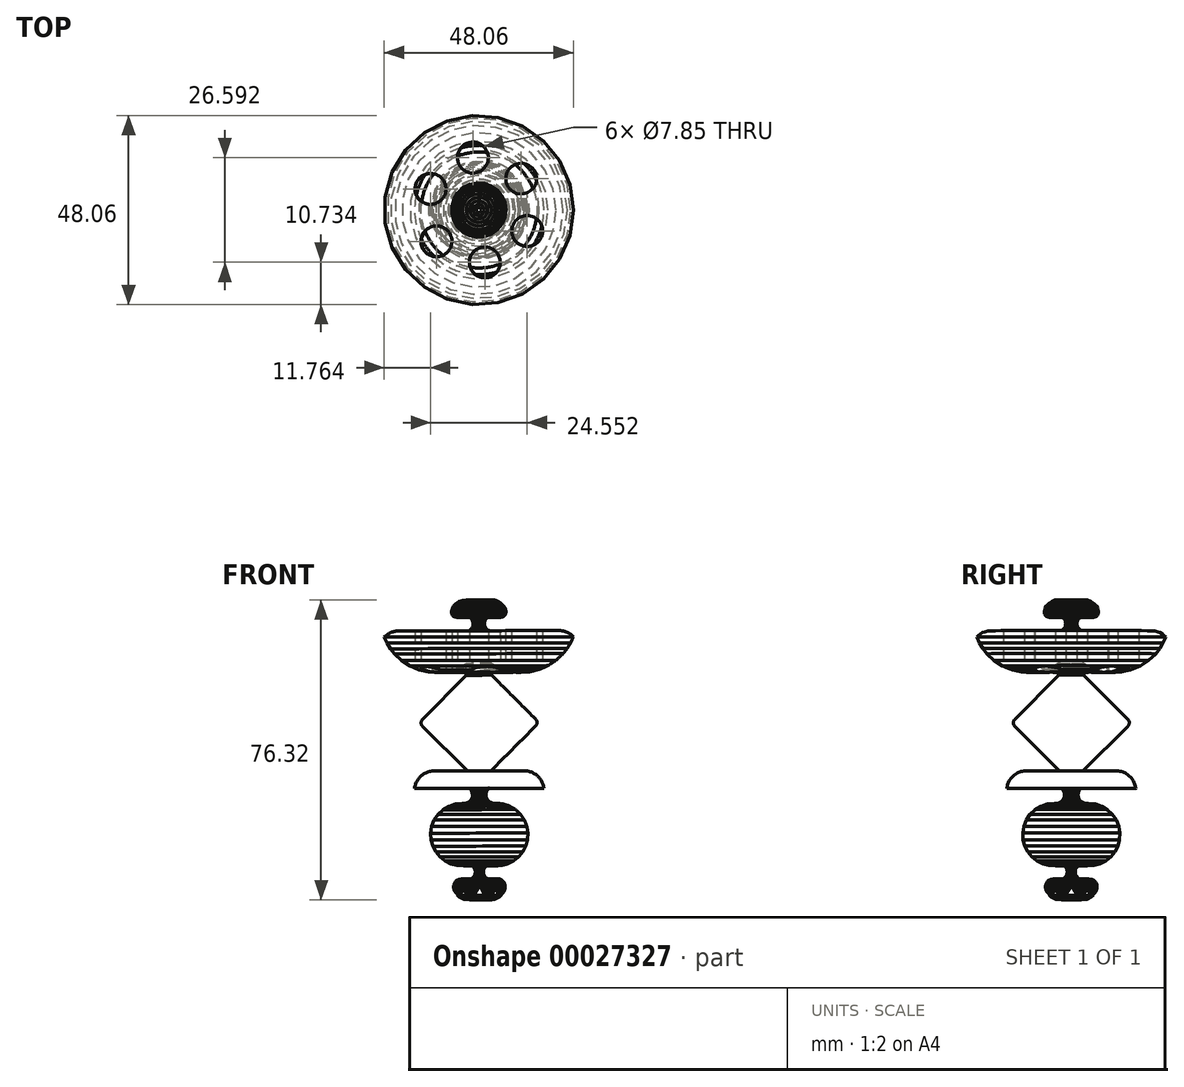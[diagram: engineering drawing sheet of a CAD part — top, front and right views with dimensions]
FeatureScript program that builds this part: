
annotation { "Feature Type Name" : "Feature", "Feature Type Description" : "" }
export const myFeature = defineFeature(function(context is Context, id is Id, definition is map)
    precondition{}
    {
        {
            var Q0;
            Q0=qCreatedBy(makeId("Front.planeOp"),FACE);
            var sketch = newSketch(context, id + "F0", { "sketchPlane" : qUnion([Q0])});
            skLineSegment(sketch, "E0", {"start": v(-12.1, 32.41) * mm, "end": v(-11.6, 14.99) * mm});
            skLineSegment(sketch, "E1", {"start": v(-11.6, 14.99) * mm, "end": v(-11.42, -2.45) * mm});
            skLineSegment(sketch, "E2", {"start": v(-11.42, -2.45) * mm, "end": v(-11.6, -19.88) * mm});
            skLineSegment(sketch, "E3", {"start": v(-11.6, -19.88) * mm, "end": v(-12.1, -37.31) * mm});
            skLineSegment(sketch, "E4", {"start": v(-12.1, -37.31) * mm, "end": v(-10.88, -37.94) * mm});
            skLineSegment(sketch, "E5", {"start": v(-10.88, -37.94) * mm, "end": v(-9.52, -38.15) * mm});
            skLineSegment(sketch, "E6", {"start": v(-9.52, -38.15) * mm, "end": v(-8.17, -37.94) * mm});
            skLineSegment(sketch, "E7", {"start": v(-8.17, -37.94) * mm, "end": v(-6.94, -37.31) * mm});
            skLineSegment(sketch, "E8", {"start": v(-6.94, -37.31) * mm, "end": v(-6.41, -36.86) * mm});
            skLineSegment(sketch, "E9", {"start": v(-6.41, -36.86) * mm, "end": v(-5.98, -36.31) * mm});
            skLineSegment(sketch, "E10", {"start": v(-5.98, -36.31) * mm, "end": v(-5.68, -35.68) * mm});
            skLineSegment(sketch, "E11", {"start": v(-5.68, -35.68) * mm, "end": v(-5.55, -35) * mm});
            skLineSegment(sketch, "E12", {"start": v(-5.55, -35) * mm, "end": v(-5.6, -34.31) * mm});
            skLineSegment(sketch, "E13", {"start": v(-5.6, -34.31) * mm, "end": v(-5.86, -33.67) * mm});
            skLineSegment(sketch, "E14", {"start": v(-5.86, -33.67) * mm, "end": v(-6.07, -33.4) * mm});
            skLineSegment(sketch, "E15", {"start": v(-6.07, -33.4) * mm, "end": v(-6.33, -33.15) * mm});
            skLineSegment(sketch, "E16", {"start": v(-6.33, -33.15) * mm, "end": v(-6.62, -32.97) * mm});
            skLineSegment(sketch, "E17", {"start": v(-6.62, -32.97) * mm, "end": v(-6.94, -32.84) * mm});
            skLineSegment(sketch, "E18", {"start": v(-6.94, -32.84) * mm, "end": v(-7.62, -32.76) * mm});
            skLineSegment(sketch, "E19", {"start": v(-7.62, -32.76) * mm, "end": v(-8.32, -32.82) * mm});
            skLineSegment(sketch, "E20", {"start": v(-8.32, -32.82) * mm, "end": v(-9, -32.9) * mm});
            skLineSegment(sketch, "E21", {"start": v(-9, -32.9) * mm, "end": v(-9.7, -32.84) * mm});
            skLineSegment(sketch, "E22", {"start": v(-9.7, -32.84) * mm, "end": v(-10.26, -32.6) * mm});
            skLineSegment(sketch, "E23", {"start": v(-10.26, -32.6) * mm, "end": v(-10.72, -32.18) * mm});
            skLineSegment(sketch, "E24", {"start": v(-10.72, -32.18) * mm, "end": v(-11.02, -31.64) * mm});
            skLineSegment(sketch, "E25", {"start": v(-11.02, -31.64) * mm, "end": v(-11.12, -31.03) * mm});
            skLineSegment(sketch, "E26", {"start": v(-11.12, -31.03) * mm, "end": v(-11.02, -30.42) * mm});
            skLineSegment(sketch, "E27", {"start": v(-11.02, -30.42) * mm, "end": v(-10.72, -29.88) * mm});
            skLineSegment(sketch, "E28", {"start": v(-10.72, -29.88) * mm, "end": v(-10.26, -29.46) * mm});
            skLineSegment(sketch, "E29", {"start": v(-10.26, -29.46) * mm, "end": v(-9.7, -29.22) * mm});
            skLineSegment(sketch, "E30", {"start": v(-9.7, -29.22) * mm, "end": v(-8.07, -29.46) * mm});
            skLineSegment(sketch, "E31", {"start": v(-8.07, -29.46) * mm, "end": v(-6.44, -29.35) * mm});
            skLineSegment(sketch, "E32", {"start": v(-6.44, -29.35) * mm, "end": v(-4.85, -28.93) * mm});
            skLineSegment(sketch, "E33", {"start": v(-4.85, -28.93) * mm, "end": v(-3.4, -28.19) * mm});
            skLineSegment(sketch, "E34", {"start": v(-3.4, -28.19) * mm, "end": v(-2.12, -27.15) * mm});
            skLineSegment(sketch, "E35", {"start": v(-2.12, -27.15) * mm, "end": v(-1.09, -25.88) * mm});
            skLineSegment(sketch, "E36", {"start": v(-1.09, -25.88) * mm, "end": v(-0.33, -24.43) * mm});
            skLineSegment(sketch, "E37", {"start": v(-0.33, -24.43) * mm, "end": v(0.12, -22.85) * mm});
            skLineSegment(sketch, "E38", {"start": v(0.12, -22.85) * mm, "end": v(0.22, -21.12) * mm});
            skLineSegment(sketch, "E39", {"start": v(0.22, -21.12) * mm, "end": v(-0.06, -19.4) * mm});
            skLineSegment(sketch, "E40", {"start": v(-0.06, -19.4) * mm, "end": v(-0.7, -17.79) * mm});
            skLineSegment(sketch, "E41", {"start": v(-0.7, -17.79) * mm, "end": v(-1.67, -16.35) * mm});
            skLineSegment(sketch, "E42", {"start": v(-1.67, -16.35) * mm, "end": v(-2.93, -15.17) * mm});
            skLineSegment(sketch, "E43", {"start": v(-2.93, -15.17) * mm, "end": v(-4.43, -14.28) * mm});
            skLineSegment(sketch, "E44", {"start": v(-4.43, -14.28) * mm, "end": v(-6.08, -13.73) * mm});
            skLineSegment(sketch, "E45", {"start": v(-6.08, -13.73) * mm, "end": v(-7.8, -13.55) * mm});
            skLineSegment(sketch, "E46", {"start": v(-7.8, -13.55) * mm, "end": v(-8.7, -13.56) * mm});
            skLineSegment(sketch, "E47", {"start": v(-8.7, -13.56) * mm, "end": v(-9.52, -13.2) * mm});
            skLineSegment(sketch, "E48", {"start": v(-9.52, -13.2) * mm, "end": v(-9.92, -12.86) * mm});
            skLineSegment(sketch, "E49", {"start": v(-9.92, -12.86) * mm, "end": v(-10.21, -12.42) * mm});
            skLineSegment(sketch, "E50", {"start": v(-10.21, -12.42) * mm, "end": v(-10.4, -11.93) * mm});
            skLineSegment(sketch, "E51", {"start": v(-10.4, -11.93) * mm, "end": v(-10.47, -11.4) * mm});
            skLineSegment(sketch, "E52", {"start": v(-10.47, -11.4) * mm, "end": v(-10.4, -10.88) * mm});
            skLineSegment(sketch, "E53", {"start": v(-10.4, -10.88) * mm, "end": v(-10.21, -10.38) * mm});
            skLineSegment(sketch, "E54", {"start": v(-10.21, -10.38) * mm, "end": v(-9.92, -9.95) * mm});
            skLineSegment(sketch, "E55", {"start": v(-9.92, -9.95) * mm, "end": v(-9.52, -9.6) * mm});
            skLineSegment(sketch, "E56", {"start": v(-9.52, -9.6) * mm, "end": v(4.25, -9.77) * mm});
            skLineSegment(sketch, "E57", {"start": v(4.25, -9.77) * mm, "end": v(4.42, -5.29) * mm});
            skLineSegment(sketch, "E58", {"start": v(4.42, -5.29) * mm, "end": v(-9.18, -5.29) * mm});
            skLineSegment(sketch, "E59", {"start": v(-9.18, -5.29) * mm, "end": v(3.05, 6.93) * mm});
            skLineSegment(sketch, "E60", {"start": v(3.05, 6.93) * mm, "end": v(-9, 18.99) * mm});
            skLineSegment(sketch, "E61", {"start": v(-9, 18.99) * mm, "end": v(-9, 21.91) * mm});
            skLineSegment(sketch, "E62", {"start": v(-9, 21.91) * mm, "end": v(-6.8, 20.77) * mm});
            skLineSegment(sketch, "E63", {"start": v(-6.8, 20.77) * mm, "end": v(-4.4, 20.03) * mm});
            skLineSegment(sketch, "E64", {"start": v(-4.4, 20.03) * mm, "end": v(-1.93, 19.71) * mm});
            skLineSegment(sketch, "E65", {"start": v(-1.93, 19.71) * mm, "end": v(0.56, 19.84) * mm});
            skLineSegment(sketch, "E66", {"start": v(0.56, 19.84) * mm, "end": v(2.99, 20.4) * mm});
            skLineSegment(sketch, "E67", {"start": v(2.99, 20.4) * mm, "end": v(5.28, 21.4) * mm});
            skLineSegment(sketch, "E68", {"start": v(5.28, 21.4) * mm, "end": v(7.37, 22.76) * mm});
            skLineSegment(sketch, "E69", {"start": v(7.37, 22.76) * mm, "end": v(9.18, 24.48) * mm});
            skLineSegment(sketch, "E70", {"start": v(9.18, 24.48) * mm, "end": v(10.2, 25.8) * mm});
            skLineSegment(sketch, "E71", {"start": v(10.2, 25.8) * mm, "end": v(11.08, 27.23) * mm});
            skLineSegment(sketch, "E72", {"start": v(11.08, 27.23) * mm, "end": v(11.77, 28.75) * mm});
            skLineSegment(sketch, "E73", {"start": v(11.77, 28.75) * mm, "end": v(12.28, 30.35) * mm});
            skLineSegment(sketch, "E74", {"start": v(12.28, 30.35) * mm, "end": v(-9.18, 30.18) * mm});
            skLineSegment(sketch, "E75", {"start": v(-9.18, 30.18) * mm, "end": v(-9.52, 30.25) * mm});
            skLineSegment(sketch, "E76", {"start": v(-9.52, 30.25) * mm, "end": v(-9.83, 30.38) * mm});
            skLineSegment(sketch, "E77", {"start": v(-9.83, 30.38) * mm, "end": v(-10.12, 30.57) * mm});
            skLineSegment(sketch, "E78", {"start": v(-10.12, 30.57) * mm, "end": v(-10.38, 30.8) * mm});
            skLineSegment(sketch, "E79", {"start": v(-10.38, 30.8) * mm, "end": v(-10.58, 31.08) * mm});
            skLineSegment(sketch, "E80", {"start": v(-10.58, 31.08) * mm, "end": v(-10.73, 31.4) * mm});
            skLineSegment(sketch, "E81", {"start": v(-10.73, 31.4) * mm, "end": v(-10.82, 31.73) * mm});
            skLineSegment(sketch, "E82", {"start": v(-10.82, 31.73) * mm, "end": v(-10.86, 32.07) * mm});
            skLineSegment(sketch, "E83", {"start": v(-10.86, 32.07) * mm, "end": v(-10.82, 32.41) * mm});
            skLineSegment(sketch, "E84", {"start": v(-10.82, 32.41) * mm, "end": v(-10.73, 32.75) * mm});
            skLineSegment(sketch, "E85", {"start": v(-10.73, 32.75) * mm, "end": v(-10.58, 33.06) * mm});
            skLineSegment(sketch, "E86", {"start": v(-10.58, 33.06) * mm, "end": v(-10.38, 33.34) * mm});
            skLineSegment(sketch, "E87", {"start": v(-10.38, 33.34) * mm, "end": v(-10.12, 33.57) * mm});
            skLineSegment(sketch, "E88", {"start": v(-10.12, 33.57) * mm, "end": v(-9.83, 33.76) * mm});
            skLineSegment(sketch, "E89", {"start": v(-9.83, 33.76) * mm, "end": v(-9.52, 33.9) * mm});
            skLineSegment(sketch, "E90", {"start": v(-9.52, 33.9) * mm, "end": v(-9.18, 33.96) * mm});
            skLineSegment(sketch, "E91", {"start": v(-9.18, 33.96) * mm, "end": v(-8.35, 33.92) * mm});
            skLineSegment(sketch, "E92", {"start": v(-8.35, 33.92) * mm, "end": v(-7.52, 33.75) * mm});
            skLineSegment(sketch, "E93", {"start": v(-7.52, 33.75) * mm, "end": v(-6.69, 33.69) * mm});
            skLineSegment(sketch, "E94", {"start": v(-6.69, 33.69) * mm, "end": v(-6.28, 33.77) * mm});
            skLineSegment(sketch, "E95", {"start": v(-6.28, 33.77) * mm, "end": v(-5.9, 33.96) * mm});
            skLineSegment(sketch, "E96", {"start": v(-5.9, 33.96) * mm, "end": v(-5.66, 34.22) * mm});
            skLineSegment(sketch, "E97", {"start": v(-5.66, 34.22) * mm, "end": v(-5.48, 34.53) * mm});
            skLineSegment(sketch, "E98", {"start": v(-5.48, 34.53) * mm, "end": v(-5.39, 34.88) * mm});
            skLineSegment(sketch, "E99", {"start": v(-5.39, 34.88) * mm, "end": v(-5.38, 35.23) * mm});
            skLineSegment(sketch, "E100", {"start": v(-5.38, 35.23) * mm, "end": v(-5.55, 35.93) * mm});
            skLineSegment(sketch, "E101", {"start": v(-5.55, 35.93) * mm, "end": v(-5.9, 36.55) * mm});
            skLineSegment(sketch, "E102", {"start": v(-5.9, 36.55) * mm, "end": v(-6.54, 37.22) * mm});
            skLineSegment(sketch, "E103", {"start": v(-6.54, 37.22) * mm, "end": v(-7.31, 37.72) * mm});
            skLineSegment(sketch, "E104", {"start": v(-7.31, 37.72) * mm, "end": v(-8.18, 38.04) * mm});
            skLineSegment(sketch, "E105", {"start": v(-8.18, 38.04) * mm, "end": v(-9.1, 38.15) * mm});
            skLineSegment(sketch, "E106", {"start": v(-9.1, 38.15) * mm, "end": v(-10, 38.04) * mm});
            skLineSegment(sketch, "E107", {"start": v(-10, 38.04) * mm, "end": v(-10.87, 37.72) * mm});
            skLineSegment(sketch, "E108", {"start": v(-10.87, 37.72) * mm, "end": v(-11.64, 37.22) * mm});
            skLineSegment(sketch, "E109", {"start": v(-11.64, 37.22) * mm, "end": v(-12.28, 36.55) * mm});
            skLineSegment(sketch, "E110", {"start": v(-12.28, 36.55) * mm, "end": v(-12.1, 32.41) * mm});
            skLineSegment(sketch, "E111", {"start": v(-12.28, 36.55) * mm, "end": v(-12.1, -37.31) * mm});
            skSolve(sketch);
        }
        {
            var Q0;
            Q0 = qSketchRegion(id + "F0", true);
            var Q1;
            Q1=sQuery(id+"F0.wireOp",EDGE,"E111");
            revolve(context, id + "F1", {"entities" : qUnion([Q0]), "axis" : qUnion([Q1]), "revolveType" : RevolveType.FULL});
        }
        {
            var Q0;
            Q0=makeQuery(id+"F1.opRevolve","SWEPT_EDGE",EDGE,{"disambiguationData":[OSD([sQuery(id+"F0.wireOp",EDGE,"E73"),sQuery(id+"F0.wireOp",EDGE,"E74")])]});
            fillet(context, id + "F2", {"entities" : qUnion([Q0]), "radius" : 5.08 * mm, "tangentPropagation" : true, "allowEdgeOverflow" : false});
        }
        {
            var Q0;
            Q0=makeQuery(id+"F1.opRevolve","SWEPT_EDGE",EDGE,{"disambiguationData":[OSD([sQuery(id+"F0.wireOp",EDGE,"E57"),sQuery(id+"F0.wireOp",EDGE,"E58")])]});
            fillet(context, id + "F3", {"entities" : qUnion([Q0]), "radius" : 5.08 * mm, "tangentPropagation" : true, "allowEdgeOverflow" : false});
        }
        {
            var Q0;
            Q0=qCreatedBy(makeId("Top.planeOp"),FACE);
            var sketch = newSketch(context, id + "F4", { "sketchPlane" : qUnion([Q0])});
            skCircle(sketch, "E112", {"center": v(-47.8, 37.52) * mm, "radius": 3.93 * mm});
            skSolve(sketch);
        }
        {
            var Q0;
            Q0=makeQuery(id+"F4.imprint","IMPRINT",FACE,{"disambiguationData":[TD([[makeQuery(id+"F4.imprint","IMPRINT",EDGE,{"derivedFrom":sQuery(id+"F4.wireOp",EDGE,"E112")}),1.0]])]});
            extrude(context, id + "F5", {"entities" : qUnion([Q0]), "depth" : 12.7 * mm});
        }
        {
            var Q0;
            Q0=makeQuery(id+"F5.opExtrude","SWEPT_BODY",BODY,{"disambiguationData":[OSD([sQuery(id+"F4.wireOp",EDGE,"E112")])]});
            transform(context, id + "F6", {"entities" : qUnion([Q0]), "transformType" : TransformType.TRANSLATION_3D, "dx" : 46.3 * mm, "dy" : -29.56 * mm, "dz" : 18.45 * mm, "makeCopy" : false});
        }
        {
            var Q0;
            Q0=makeQuery(id+"F5.opExtrude","SWEPT_BODY",BODY,{"disambiguationData":[OSD([sQuery(id+"F4.wireOp",EDGE,"E112")])]});
            var Q1;
            Q1=makeQuery(id+"F2.opFillet","BLEND_EDGE",EDGE,{"blendedFrom":[makeQuery(id+"F1.opRevolve","SWEPT_EDGE",EDGE,{"disambiguationData":[OSD([sQuery(id+"F0.wireOp",EDGE,"E73"),sQuery(id+"F0.wireOp",EDGE,"E74")])]}),makeQuery(id+"F1.opRevolve","SWEPT_FACE",FACE,{"disambiguationData":[OSD([sQuery(id+"F0.wireOp",EDGE,"E72")])]})],"blendedInto":[makeQuery(id+"F1.opRevolve","SWEPT_FACE",FACE,{"disambiguationData":[OSD([sQuery(id+"F0.wireOp",EDGE,"E72")])]})]});
            circularPattern(context, id + "F7", {"entities" : qUnion([Q0]), "axis" : qUnion([Q1]), "angle" : 360 * degree, "instanceCount" : 6, "equalSpace" : true});
        }
        {
            var Q0;
            Q0=makeQuery(id+"F7.opPattern","COPY",BODY,{"derivedFrom":makeQuery(id+"F5.opExtrude","SWEPT_BODY",BODY,{"disambiguationData":[OSD([sQuery(id+"F4.wireOp",EDGE,"E112")])]}),"instanceName":"4"});
            var Q1;
            Q1=makeQuery(id+"F7.opPattern","COPY",BODY,{"derivedFrom":makeQuery(id+"F5.opExtrude","SWEPT_BODY",BODY,{"disambiguationData":[OSD([sQuery(id+"F4.wireOp",EDGE,"E112")])]}),"instanceName":"5"});
            var Q2;
            Q2=makeQuery(id+"F5.opExtrude","SWEPT_BODY",BODY,{"disambiguationData":[OSD([sQuery(id+"F4.wireOp",EDGE,"E112")])]});
            var Q3;
            Q3=makeQuery(id+"F7.opPattern","COPY",BODY,{"derivedFrom":makeQuery(id+"F5.opExtrude","SWEPT_BODY",BODY,{"disambiguationData":[OSD([sQuery(id+"F4.wireOp",EDGE,"E112")])]}),"instanceName":"1"});
            var Q4;
            Q4=makeQuery(id+"F7.opPattern","COPY",BODY,{"derivedFrom":makeQuery(id+"F5.opExtrude","SWEPT_BODY",BODY,{"disambiguationData":[OSD([sQuery(id+"F4.wireOp",EDGE,"E112")])]}),"instanceName":"2"});
            var Q5;
            Q5=makeQuery(id+"F7.opPattern","COPY",BODY,{"derivedFrom":makeQuery(id+"F5.opExtrude","SWEPT_BODY",BODY,{"disambiguationData":[OSD([sQuery(id+"F4.wireOp",EDGE,"E112")])]}),"instanceName":"3"});
            var Q6;
            Q6=makeQuery(id+"F1.opRevolve","SWEPT_BODY",BODY,{"disambiguationData":[OSD([sQuery(id+"F0.wireOp",EDGE,"E4"),sQuery(id+"F0.wireOp",EDGE,"E5"),sQuery(id+"F0.wireOp",EDGE,"E6"),sQuery(id+"F0.wireOp",EDGE,"E7"),sQuery(id+"F0.wireOp",EDGE,"E8"),sQuery(id+"F0.wireOp",EDGE,"E9"),sQuery(id+"F0.wireOp",EDGE,"E10"),sQuery(id+"F0.wireOp",EDGE,"E11"),sQuery(id+"F0.wireOp",EDGE,"E12"),sQuery(id+"F0.wireOp",EDGE,"E13"),sQuery(id+"F0.wireOp",EDGE,"E14"),sQuery(id+"F0.wireOp",EDGE,"E15"),sQuery(id+"F0.wireOp",EDGE,"E16"),sQuery(id+"F0.wireOp",EDGE,"E17"),sQuery(id+"F0.wireOp",EDGE,"E18"),sQuery(id+"F0.wireOp",EDGE,"E19"),sQuery(id+"F0.wireOp",EDGE,"E20"),sQuery(id+"F0.wireOp",EDGE,"E21"),sQuery(id+"F0.wireOp",EDGE,"E22"),sQuery(id+"F0.wireOp",EDGE,"E23"),sQuery(id+"F0.wireOp",EDGE,"E24"),sQuery(id+"F0.wireOp",EDGE,"E25"),sQuery(id+"F0.wireOp",EDGE,"E26"),sQuery(id+"F0.wireOp",EDGE,"E27"),sQuery(id+"F0.wireOp",EDGE,"E28"),sQuery(id+"F0.wireOp",EDGE,"E29"),sQuery(id+"F0.wireOp",EDGE,"E30"),sQuery(id+"F0.wireOp",EDGE,"E31"),sQuery(id+"F0.wireOp",EDGE,"E32"),sQuery(id+"F0.wireOp",EDGE,"E33"),sQuery(id+"F0.wireOp",EDGE,"E34"),sQuery(id+"F0.wireOp",EDGE,"E35"),sQuery(id+"F0.wireOp",EDGE,"E36"),sQuery(id+"F0.wireOp",EDGE,"E37"),sQuery(id+"F0.wireOp",EDGE,"E38"),sQuery(id+"F0.wireOp",EDGE,"E39"),sQuery(id+"F0.wireOp",EDGE,"E40"),sQuery(id+"F0.wireOp",EDGE,"E41"),sQuery(id+"F0.wireOp",EDGE,"E42"),sQuery(id+"F0.wireOp",EDGE,"E43"),sQuery(id+"F0.wireOp",EDGE,"E44"),sQuery(id+"F0.wireOp",EDGE,"E45"),sQuery(id+"F0.wireOp",EDGE,"E46"),sQuery(id+"F0.wireOp",EDGE,"E47"),sQuery(id+"F0.wireOp",EDGE,"E48"),sQuery(id+"F0.wireOp",EDGE,"E49"),sQuery(id+"F0.wireOp",EDGE,"E50"),sQuery(id+"F0.wireOp",EDGE,"E51"),sQuery(id+"F0.wireOp",EDGE,"E52"),sQuery(id+"F0.wireOp",EDGE,"E53"),sQuery(id+"F0.wireOp",EDGE,"E54"),sQuery(id+"F0.wireOp",EDGE,"E55"),sQuery(id+"F0.wireOp",EDGE,"E56"),sQuery(id+"F0.wireOp",EDGE,"E57"),sQuery(id+"F0.wireOp",EDGE,"E58"),sQuery(id+"F0.wireOp",EDGE,"E59"),sQuery(id+"F0.wireOp",EDGE,"E60"),sQuery(id+"F0.wireOp",EDGE,"E61"),sQuery(id+"F0.wireOp",EDGE,"E62"),sQuery(id+"F0.wireOp",EDGE,"E63"),sQuery(id+"F0.wireOp",EDGE,"E64"),sQuery(id+"F0.wireOp",EDGE,"E65"),sQuery(id+"F0.wireOp",EDGE,"E66"),sQuery(id+"F0.wireOp",EDGE,"E67"),sQuery(id+"F0.wireOp",EDGE,"E68"),sQuery(id+"F0.wireOp",EDGE,"E69"),sQuery(id+"F0.wireOp",EDGE,"E70"),sQuery(id+"F0.wireOp",EDGE,"E71"),sQuery(id+"F0.wireOp",EDGE,"E72"),sQuery(id+"F0.wireOp",EDGE,"E73"),sQuery(id+"F0.wireOp",EDGE,"E74"),sQuery(id+"F0.wireOp",EDGE,"E75"),sQuery(id+"F0.wireOp",EDGE,"E76"),sQuery(id+"F0.wireOp",EDGE,"E77"),sQuery(id+"F0.wireOp",EDGE,"E78"),sQuery(id+"F0.wireOp",EDGE,"E79"),sQuery(id+"F0.wireOp",EDGE,"E80"),sQuery(id+"F0.wireOp",EDGE,"E81"),sQuery(id+"F0.wireOp",EDGE,"E82"),sQuery(id+"F0.wireOp",EDGE,"E83"),sQuery(id+"F0.wireOp",EDGE,"E84"),sQuery(id+"F0.wireOp",EDGE,"E85"),sQuery(id+"F0.wireOp",EDGE,"E86"),sQuery(id+"F0.wireOp",EDGE,"E87"),sQuery(id+"F0.wireOp",EDGE,"E88"),sQuery(id+"F0.wireOp",EDGE,"E89"),sQuery(id+"F0.wireOp",EDGE,"E90"),sQuery(id+"F0.wireOp",EDGE,"E91"),sQuery(id+"F0.wireOp",EDGE,"E92"),sQuery(id+"F0.wireOp",EDGE,"E93"),sQuery(id+"F0.wireOp",EDGE,"E94"),sQuery(id+"F0.wireOp",EDGE,"E95"),sQuery(id+"F0.wireOp",EDGE,"E96"),sQuery(id+"F0.wireOp",EDGE,"E97"),sQuery(id+"F0.wireOp",EDGE,"E98"),sQuery(id+"F0.wireOp",EDGE,"E99"),sQuery(id+"F0.wireOp",EDGE,"E100"),sQuery(id+"F0.wireOp",EDGE,"E101"),sQuery(id+"F0.wireOp",EDGE,"E102"),sQuery(id+"F0.wireOp",EDGE,"E103"),sQuery(id+"F0.wireOp",EDGE,"E104"),sQuery(id+"F0.wireOp",EDGE,"E105"),sQuery(id+"F0.wireOp",EDGE,"E106"),sQuery(id+"F0.wireOp",EDGE,"E107"),sQuery(id+"F0.wireOp",EDGE,"E108"),sQuery(id+"F0.wireOp",EDGE,"E109"),sQuery(id+"F0.wireOp",EDGE,"E111")])]});
            booleanBodies(context, id + "F8", {"operationType" : BooleanOperationType.SUBTRACTION, "tools" : qUnion([Q0, Q1, Q2, Q3, Q4, Q5]), "targets" : qUnion([Q6])});
        }
        {
            var Q0;
            Q0=qCreatedBy(makeId("Right.planeOp"),FACE);
            var sketch = newSketch(context, id + "F9", { "sketchPlane" : qUnion([Q0])});
            skCircle(sketch, "E113.cCircle", {"center": v(0, -76.2) * mm, "radius": 1.71 * mm, "construction": true});
            skLineSegment(sketch, "E113.0", {"start": v(0, -74.49) * mm, "end": v(1.48, -77.06) * mm});
            skLineSegment(sketch, "E113.1", {"start": v(1.48, -77.06) * mm, "end": v(-1.48, -77.06) * mm});
            skLineSegment(sketch, "E113.2", {"start": v(-1.48, -77.06) * mm, "end": v(0, -74.49) * mm});
            skSolve(sketch);
        }
        {
            var Q0;
            Q0=makeQuery(id+"F9.imprint","IMPRINT",FACE,{"disambiguationData":[TD([[makeQuery(id+"F9.imprint","IMPRINT",EDGE,{"derivedFrom":sQuery(id+"F9.wireOp",EDGE,"E113.0")}),-1.0]])]});
            extrude(context, id + "F10", {"entities" : qUnion([Q0]), "depth" : 6.35 * mm});
        }
        {
            var Q0;
            Q0=makeQuery(id+"F10.opExtrude","SWEPT_BODY",BODY,{"disambiguationData":[OSD([sQuery(id+"F9.wireOp",EDGE,"E113.0"),sQuery(id+"F9.wireOp",EDGE,"E113.1"),sQuery(id+"F9.wireOp",EDGE,"E113.2")])]});
            transform(context, id + "F11", {"entities" : qUnion([Q0]), "transformType" : TransformType.TRANSLATION_3D, "dx" : -6.65 * mm, "dy" : 0 * mm, "dz" : 40.1 * mm, "makeCopy" : false});
        }
        {
            var Q0;
            Q0=makeQuery(id+"F10.opExtrude","SWEPT_BODY",BODY,{"disambiguationData":[OSD([sQuery(id+"F9.wireOp",EDGE,"E113.0"),sQuery(id+"F9.wireOp",EDGE,"E113.1"),sQuery(id+"F9.wireOp",EDGE,"E113.2")])]});
            var Q1;
            Q1=makeQuery(id+"F1.opRevolve","SWEPT_EDGE",EDGE,{"disambiguationData":[OSD([sQuery(id+"F0.wireOp",EDGE,"E5"),sQuery(id+"F0.wireOp",EDGE,"E6")])]});
            circularPattern(context, id + "F12", {"entities" : qUnion([Q0]), "axis" : qUnion([Q1]), "angle" : 360 * degree, "instanceCount" : 8, "equalSpace" : true});
        }
        {
            var Q0;
            Q0=makeQuery(id+"F10.opExtrude","SWEPT_BODY",BODY,{"disambiguationData":[OSD([sQuery(id+"F9.wireOp",EDGE,"E113.0"),sQuery(id+"F9.wireOp",EDGE,"E113.1"),sQuery(id+"F9.wireOp",EDGE,"E113.2")])]});
            var Q1;
            Q1=makeQuery(id+"F12.opPattern","COPY",BODY,{"derivedFrom":makeQuery(id+"F10.opExtrude","SWEPT_BODY",BODY,{"disambiguationData":[OSD([sQuery(id+"F9.wireOp",EDGE,"E113.0"),sQuery(id+"F9.wireOp",EDGE,"E113.1"),sQuery(id+"F9.wireOp",EDGE,"E113.2")])]}),"instanceName":"1"});
            var Q2;
            Q2=makeQuery(id+"F12.opPattern","COPY",BODY,{"derivedFrom":makeQuery(id+"F10.opExtrude","SWEPT_BODY",BODY,{"disambiguationData":[OSD([sQuery(id+"F9.wireOp",EDGE,"E113.0"),sQuery(id+"F9.wireOp",EDGE,"E113.1"),sQuery(id+"F9.wireOp",EDGE,"E113.2")])]}),"instanceName":"2"});
            var Q3;
            Q3=makeQuery(id+"F12.opPattern","COPY",BODY,{"derivedFrom":makeQuery(id+"F10.opExtrude","SWEPT_BODY",BODY,{"disambiguationData":[OSD([sQuery(id+"F9.wireOp",EDGE,"E113.0"),sQuery(id+"F9.wireOp",EDGE,"E113.1"),sQuery(id+"F9.wireOp",EDGE,"E113.2")])]}),"instanceName":"3"});
            var Q4;
            Q4=makeQuery(id+"F12.opPattern","COPY",BODY,{"derivedFrom":makeQuery(id+"F10.opExtrude","SWEPT_BODY",BODY,{"disambiguationData":[OSD([sQuery(id+"F9.wireOp",EDGE,"E113.0"),sQuery(id+"F9.wireOp",EDGE,"E113.1"),sQuery(id+"F9.wireOp",EDGE,"E113.2")])]}),"instanceName":"4"});
            var Q5;
            Q5=makeQuery(id+"F12.opPattern","COPY",BODY,{"derivedFrom":makeQuery(id+"F10.opExtrude","SWEPT_BODY",BODY,{"disambiguationData":[OSD([sQuery(id+"F9.wireOp",EDGE,"E113.0"),sQuery(id+"F9.wireOp",EDGE,"E113.1"),sQuery(id+"F9.wireOp",EDGE,"E113.2")])]}),"instanceName":"5"});
            var Q6;
            Q6=makeQuery(id+"F12.opPattern","COPY",BODY,{"derivedFrom":makeQuery(id+"F10.opExtrude","SWEPT_BODY",BODY,{"disambiguationData":[OSD([sQuery(id+"F9.wireOp",EDGE,"E113.0"),sQuery(id+"F9.wireOp",EDGE,"E113.1"),sQuery(id+"F9.wireOp",EDGE,"E113.2")])]}),"instanceName":"6"});
            var Q7;
            Q7=makeQuery(id+"F12.opPattern","COPY",BODY,{"derivedFrom":makeQuery(id+"F10.opExtrude","SWEPT_BODY",BODY,{"disambiguationData":[OSD([sQuery(id+"F9.wireOp",EDGE,"E113.0"),sQuery(id+"F9.wireOp",EDGE,"E113.1"),sQuery(id+"F9.wireOp",EDGE,"E113.2")])]}),"instanceName":"7"});
            var Q8;
            Q8=makeQuery(id+"F1.opRevolve","SWEPT_BODY",BODY,{"disambiguationData":[OSD([sQuery(id+"F0.wireOp",EDGE,"E4"),sQuery(id+"F0.wireOp",EDGE,"E5"),sQuery(id+"F0.wireOp",EDGE,"E6"),sQuery(id+"F0.wireOp",EDGE,"E7"),sQuery(id+"F0.wireOp",EDGE,"E8"),sQuery(id+"F0.wireOp",EDGE,"E9"),sQuery(id+"F0.wireOp",EDGE,"E10"),sQuery(id+"F0.wireOp",EDGE,"E11"),sQuery(id+"F0.wireOp",EDGE,"E12"),sQuery(id+"F0.wireOp",EDGE,"E13"),sQuery(id+"F0.wireOp",EDGE,"E14"),sQuery(id+"F0.wireOp",EDGE,"E15"),sQuery(id+"F0.wireOp",EDGE,"E16"),sQuery(id+"F0.wireOp",EDGE,"E17"),sQuery(id+"F0.wireOp",EDGE,"E18"),sQuery(id+"F0.wireOp",EDGE,"E19"),sQuery(id+"F0.wireOp",EDGE,"E20"),sQuery(id+"F0.wireOp",EDGE,"E21"),sQuery(id+"F0.wireOp",EDGE,"E22"),sQuery(id+"F0.wireOp",EDGE,"E23"),sQuery(id+"F0.wireOp",EDGE,"E24"),sQuery(id+"F0.wireOp",EDGE,"E25"),sQuery(id+"F0.wireOp",EDGE,"E26"),sQuery(id+"F0.wireOp",EDGE,"E27"),sQuery(id+"F0.wireOp",EDGE,"E28"),sQuery(id+"F0.wireOp",EDGE,"E29"),sQuery(id+"F0.wireOp",EDGE,"E30"),sQuery(id+"F0.wireOp",EDGE,"E31"),sQuery(id+"F0.wireOp",EDGE,"E32"),sQuery(id+"F0.wireOp",EDGE,"E33"),sQuery(id+"F0.wireOp",EDGE,"E34"),sQuery(id+"F0.wireOp",EDGE,"E35"),sQuery(id+"F0.wireOp",EDGE,"E36"),sQuery(id+"F0.wireOp",EDGE,"E37"),sQuery(id+"F0.wireOp",EDGE,"E38"),sQuery(id+"F0.wireOp",EDGE,"E39"),sQuery(id+"F0.wireOp",EDGE,"E40"),sQuery(id+"F0.wireOp",EDGE,"E41"),sQuery(id+"F0.wireOp",EDGE,"E42"),sQuery(id+"F0.wireOp",EDGE,"E43"),sQuery(id+"F0.wireOp",EDGE,"E44"),sQuery(id+"F0.wireOp",EDGE,"E45"),sQuery(id+"F0.wireOp",EDGE,"E46"),sQuery(id+"F0.wireOp",EDGE,"E47"),sQuery(id+"F0.wireOp",EDGE,"E48"),sQuery(id+"F0.wireOp",EDGE,"E49"),sQuery(id+"F0.wireOp",EDGE,"E50"),sQuery(id+"F0.wireOp",EDGE,"E51"),sQuery(id+"F0.wireOp",EDGE,"E52"),sQuery(id+"F0.wireOp",EDGE,"E53"),sQuery(id+"F0.wireOp",EDGE,"E54"),sQuery(id+"F0.wireOp",EDGE,"E55"),sQuery(id+"F0.wireOp",EDGE,"E56"),sQuery(id+"F0.wireOp",EDGE,"E57"),sQuery(id+"F0.wireOp",EDGE,"E58"),sQuery(id+"F0.wireOp",EDGE,"E59"),sQuery(id+"F0.wireOp",EDGE,"E60"),sQuery(id+"F0.wireOp",EDGE,"E61"),sQuery(id+"F0.wireOp",EDGE,"E62"),sQuery(id+"F0.wireOp",EDGE,"E63"),sQuery(id+"F0.wireOp",EDGE,"E64"),sQuery(id+"F0.wireOp",EDGE,"E65"),sQuery(id+"F0.wireOp",EDGE,"E66"),sQuery(id+"F0.wireOp",EDGE,"E67"),sQuery(id+"F0.wireOp",EDGE,"E68"),sQuery(id+"F0.wireOp",EDGE,"E69"),sQuery(id+"F0.wireOp",EDGE,"E70"),sQuery(id+"F0.wireOp",EDGE,"E71"),sQuery(id+"F0.wireOp",EDGE,"E72"),sQuery(id+"F0.wireOp",EDGE,"E73"),sQuery(id+"F0.wireOp",EDGE,"E74"),sQuery(id+"F0.wireOp",EDGE,"E75"),sQuery(id+"F0.wireOp",EDGE,"E76"),sQuery(id+"F0.wireOp",EDGE,"E77"),sQuery(id+"F0.wireOp",EDGE,"E78"),sQuery(id+"F0.wireOp",EDGE,"E79"),sQuery(id+"F0.wireOp",EDGE,"E80"),sQuery(id+"F0.wireOp",EDGE,"E81"),sQuery(id+"F0.wireOp",EDGE,"E82"),sQuery(id+"F0.wireOp",EDGE,"E83"),sQuery(id+"F0.wireOp",EDGE,"E84"),sQuery(id+"F0.wireOp",EDGE,"E85"),sQuery(id+"F0.wireOp",EDGE,"E86"),sQuery(id+"F0.wireOp",EDGE,"E87"),sQuery(id+"F0.wireOp",EDGE,"E88"),sQuery(id+"F0.wireOp",EDGE,"E89"),sQuery(id+"F0.wireOp",EDGE,"E90"),sQuery(id+"F0.wireOp",EDGE,"E91"),sQuery(id+"F0.wireOp",EDGE,"E92"),sQuery(id+"F0.wireOp",EDGE,"E93"),sQuery(id+"F0.wireOp",EDGE,"E94"),sQuery(id+"F0.wireOp",EDGE,"E95"),sQuery(id+"F0.wireOp",EDGE,"E96"),sQuery(id+"F0.wireOp",EDGE,"E97"),sQuery(id+"F0.wireOp",EDGE,"E98"),sQuery(id+"F0.wireOp",EDGE,"E99"),sQuery(id+"F0.wireOp",EDGE,"E100"),sQuery(id+"F0.wireOp",EDGE,"E101"),sQuery(id+"F0.wireOp",EDGE,"E102"),sQuery(id+"F0.wireOp",EDGE,"E103"),sQuery(id+"F0.wireOp",EDGE,"E104"),sQuery(id+"F0.wireOp",EDGE,"E105"),sQuery(id+"F0.wireOp",EDGE,"E106"),sQuery(id+"F0.wireOp",EDGE,"E107"),sQuery(id+"F0.wireOp",EDGE,"E108"),sQuery(id+"F0.wireOp",EDGE,"E109"),sQuery(id+"F0.wireOp",EDGE,"E111")])]});
            booleanBodies(context, id + "F13", {"operationType" : BooleanOperationType.SUBTRACTION, "tools" : qUnion([Q0, Q1, Q2, Q3, Q4, Q5, Q6, Q7]), "targets" : qUnion([Q8])});
        }
        {
            var Q0;
            Q0=makeQuery(id+"F1.opRevolve","SWEPT_EDGE",EDGE,{"disambiguationData":[OSD([sQuery(id+"F0.wireOp",EDGE,"E59"),sQuery(id+"F0.wireOp",EDGE,"E60")])]});
            fillet(context, id + "F14", {"entities" : qUnion([Q0]), "radius" : 1.27 * mm, "tangentPropagation" : true, "allowEdgeOverflow" : false});
        }
    });
